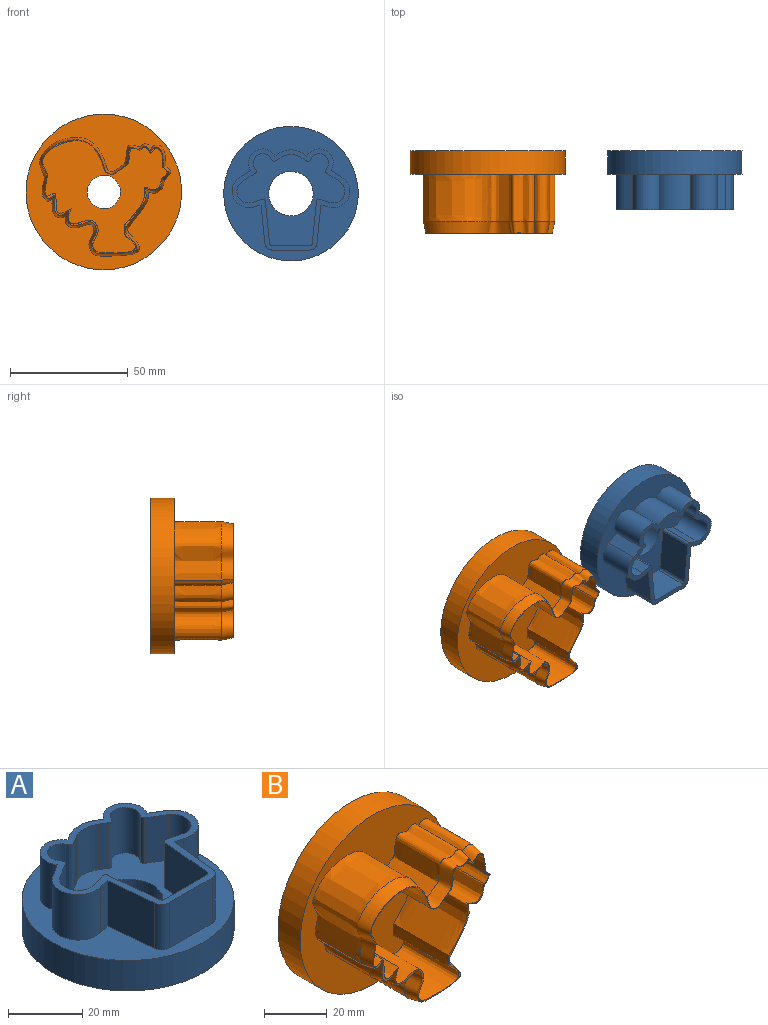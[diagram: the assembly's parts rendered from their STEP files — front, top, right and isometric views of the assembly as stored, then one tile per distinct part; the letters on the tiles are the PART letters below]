
ASSEMBLY  parts=2 mates=1
PART A: 46 faces, bbox 57.2x57.2x25 mm
  f0: plane 15x4.29mm, normal (0.31,0.95,0), area 67.6mm2, adj f1,f39,f40,f45
  f1: cylinder r=1mm len=15mm, axis (0,0,-1), area 26.7mm2, adj f0,f2,f40,f45
  f2: plane 17.87x15mm, normal (-1,0.1,0), area 269.4mm2, adj f1,f3,f40,f45
  f3: cylinder r=1mm len=15mm, axis (0,0,-1), area 22.1mm2, adj f2,f4,f40,f45
  f4: plane 16.19x15mm, normal (0,1,0), area 242.9mm2, adj f3,f5,f40,f45
  f5: cylinder r=1mm len=15mm, axis (0,0,-1), area 22.1mm2, adj f4,f6,f40,f45
  f6: plane 17.87x15mm, normal (1,0.1,0), area 269.4mm2, adj f5,f7,f40,f45
  f7: cylinder r=1mm len=15mm, axis (0,0,-1), area 26.7mm2, adj f6,f8,f40,f45
  f8: plane 15x4.29mm, normal (-0.31,0.95,0), area 67.6mm2, adj f7,f9,f40,f45
  f9: cylinder r=5mm len=15mm, axis (0,0,-1), area 217.5mm2, adj f8,f10,f40,f45
  f10: plane 15x5.5mm, normal (0.53,-0.85,0), area 96.9mm2, adj f9,f11,f40,f45
  f11: cylinder r=1mm len=15mm, axis (0,0,-1), area 23.6mm2, adj f10,f12,f40,f45
  f12: plane 15x0.37mm, normal (0.85,0.53,0), area 6.6mm2, adj f11,f13,f40,f45
  f13: cylinder r=4mm len=15mm, axis (0,0,-1), area 197.7mm2, adj f12,f14,f40,f45
  f14: plane 15x0.9mm, normal (-0.85,-0.53,0), area 15.8mm2, adj f13,f15,f40,f45
  f15: cylinder r=1mm len=15mm, axis (0,0,-1), area 23.6mm2, adj f14,f16,f40,f45
  f16: plane 15x2.46mm, normal (0.53,-0.85,0), area 43.4mm2, adj f15,f17,f40,f45
  f17: cylinder r=8mm len=15mm, axis (0,0,-1), area 132.8mm2, adj f16,f18,f40,f45
  f18: plane 15x2.46mm, normal (-0.53,-0.85,0), area 43.4mm2, adj f17,f19,f40,f45
  f19: cylinder r=1mm len=15mm, axis (0,0,-1), area 23.6mm2, adj f18,f20,f40,f45
  f20: plane 15x0.9mm, normal (0.85,-0.53,0), area 15.8mm2, adj f19,f21,f40,f45
  f21: cylinder r=4mm len=15mm, axis (0,0,-1), area 197.7mm2, adj f20,f22,f40,f45
  f22: plane 15x0.37mm, normal (-0.85,0.53,0), area 6.6mm2, adj f21,f23,f40,f45
  f23: cylinder r=1mm len=15mm, axis (0,0,-1), area 23.6mm2, adj f22,f24,f40,f45
  f24: plane 15x5.5mm, normal (-0.53,-0.85,0), area 96.9mm2, adj f23,f39,f40,f45
  f25: cylinder r=7mm len=15mm, axis (0,0,-1), area 301mm2, adj f26,f38,f40,f41
  f26: plane 15x3.35mm, normal (0.25,-0.97,0), area 51.9mm2, adj f25,f27,f40,f41
  f27: plane 16.43x15mm, normal (-1,-0.1,0), area 247.6mm2, adj f26,f28,f40,f41
  f28: cylinder r=3mm len=15mm, axis (0,0,-1), area 66.2mm2, adj f27,f29,f40,f41
  f29: plane 16.19x15mm, normal (0,-1,0), area 242.9mm2, adj f28,f30,f40,f41
  f30: cylinder r=3mm len=15mm, axis (0,0,-1), area 66.2mm2, adj f29,f31,f40,f41
  f31: plane 16.43x15mm, normal (1,-0.1,0), area 247.6mm2, adj f30,f32,f40,f41
  f32: plane 15x2.81mm, normal (-0.24,-0.97,0), area 43.4mm2, adj f31,f33,f40,f41
  f33: cylinder r=7mm len=15mm, axis (0,0,-1), area 309.5mm2, adj f32,f34,f40,f41
  f34: plane 15x4.6mm, normal (0.53,0.85,0), area 81.2mm2, adj f33,f35,f40,f41
  f35: cylinder r=6mm len=15mm, axis (0,0,-1), area 287.1mm2, adj f34,f36,f40,f41
  f36: cylinder r=10mm len=15mm, axis (0,0,-1), area 223.3mm2, adj f35,f37,f40,f41
  f37: cylinder r=6mm len=15mm, axis (0,0,-1), area 287.1mm2, adj f36,f38,f40,f41
  f38: plane 15x4.6mm, normal (-0.53,0.85,0), area 81.2mm2, adj f25,f37,f40,f41
  f39: cylinder r=5mm len=15mm, axis (0,0,-1), area 217.5mm2, adj f0,f24,f40,f45
  f40: plane 50x43mm, normal (0,0,1), area 331mm2, adj f0,f1,f2,f3,f4,f5,f6,f7
  f41: plane 57.18x57.18mm, normal (0,0,1), area 1141.4mm2, adj f25,f26,f27,f28,f29,f30,f31,f32
  f42: cylinder r=28.59mm len=57.18mm, axis (0,0,1), area 1796.4mm2, adj f41,f44
  f43: cylinder r=9.44mm len=18.88mm, axis (0,0,1), area 593.3mm2, adj f44,f45
  f44: plane 57.18x57.18mm, normal (0,0,-1), area 2287.8mm2, adj f42,f43
  f45: plane 46x39mm, normal (0,0,1), area 815.5mm2, adj f0,f1,f2,f3,f4,f5,f6,f7
PART B: 25 faces, bbox 67.4x36.2x67.4 mm
  f0: plane 19.79x14.1mm, normal (0,-1,0), area 7.5mm2, adj f2,f3,f4,f5,f12,f17,f18,f19
  f1: extruded ~36.61x30.8mm, area 2057.5mm2, adj f2,f12,f13,f24
  f2: extruded ~25x6.6mm, area 260.3mm2, adj f0,f1,f3,f13,f17,f24
  f3: extruded ~25x4.49mm, area 156.4mm2, adj f0,f2,f4,f24
  f4: extruded ~25x8.09mm, area 320.3mm2, adj f0,f3,f5,f24
  f5: extruded ~25x4.35mm, area 150.3mm2, adj f0,f4,f12,f24
  f6: extruded ~47.25x24.91mm, area 1707mm2, adj f7,f11,f17,f20
  f7: extruded ~20x3.94mm, area 101.6mm2, adj f6,f8,f15,f20
  f8: extruded ~20x7.82mm, area 246.8mm2, adj f7,f9,f14,f20
  f9: extruded ~35.26x27.55mm, area 1553.3mm2, adj f8,f10,f16,f20
  f10: extruded ~20x11.49mm, area 364.2mm2, adj f9,f11,f18,f20
  f11: extruded ~20x9mm, area 277.3mm2, adj f6,f10,f19,f20
  f12: extruded ~39.89x32mm, area 2258.1mm2, adj f0,f1,f5,f13,f16,f18,f24
  f13: plane 49.73x45.67mm, normal (0,-1,0), area 51mm2, adj f1,f2,f12,f14,f15,f16,f17
  f14: bspline ~10.43x8.41mm, area 67.9mm2, adj f8,f13,f15,f16
  f15: bspline ~5.56x5mm, area 25.8mm2, adj f7,f13,f14,f17
  f16: bspline ~35.29x29.86mm, area 408.8mm2, adj f9,f12,f13,f14,f18
  f17: bspline ~47.84x24.97mm, area 419.5mm2, adj f0,f2,f6,f13,f15,f19
  f18: bspline ~12.33x12.12mm, area 89.7mm2, adj f0,f10,f12,f16,f19
  f19: bspline ~10.2x7.93mm, area 69.4mm2, adj f0,f11,f17,f18
  f20: plane 66.2x66.2mm, normal (0,-1,0), area 1699.8mm2, adj f6,f7,f8,f9,f10,f11,f21
  f21: cylinder r=33.1mm len=66.2mm, axis (0,-1,0), area 2079.9mm2, adj f20,f23
  f22: cylinder r=7.09mm len=14.17mm, axis (0,-1,0), area 445.3mm2, adj f23,f24
  f23: plane 66.2x66.2mm, normal (0,1,0), area 3284.6mm2, adj f21,f22
  f24: plane 53.45x48.09mm, normal (0,-1,0), area 1289.5mm2, adj f1,f2,f3,f4,f5,f12,f22
PLACE A rot(axis=(1,0,0),90deg) t=(62.49,72.72,90.95)mm
PLACE B t=(-13.99,72.72,105.14)mm
MATE planar A.f45 <-> B.f24  axis (0,-1,0) through (62.49,72.72,98.65)mm
